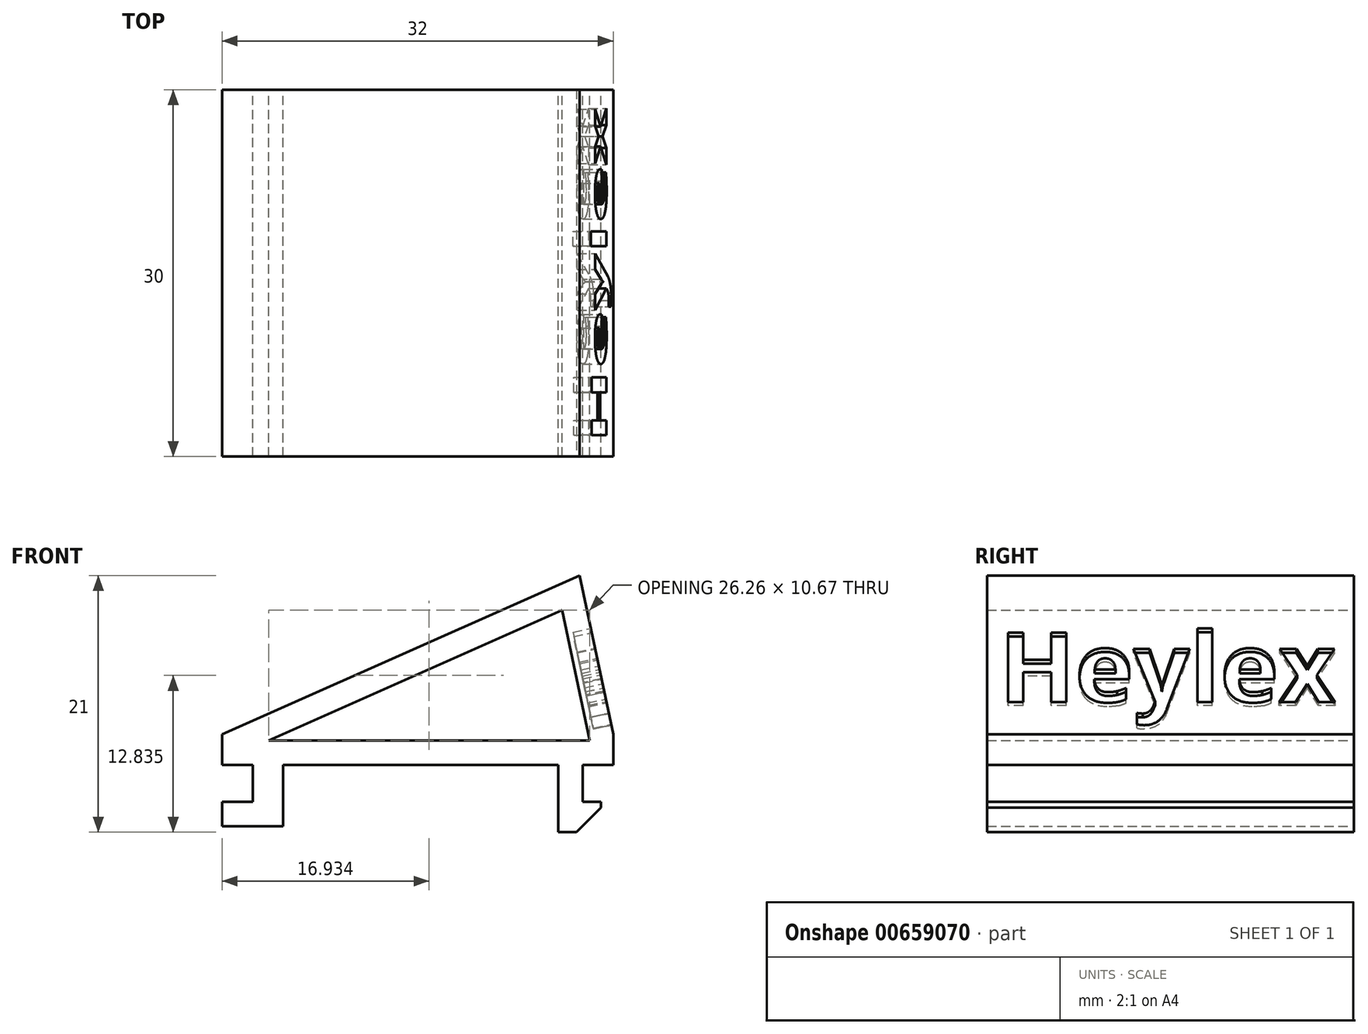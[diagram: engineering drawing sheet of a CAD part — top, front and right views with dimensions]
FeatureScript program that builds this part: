
annotation { "Feature Type Name" : "Feature", "Feature Type Description" : "" }
export const myFeature = defineFeature(function(context is Context, id is Id, definition is map)
    precondition{}
    {
        {
            var Q0;
            Q0=qCreatedBy(makeId("Front.planeOp"),FACE);
            var sketch = newSketch(context, id + "F0", { "sketchPlane" : qUnion([Q0])});
            skLineSegment(sketch, "E0.left", {"start": v(-16.03, 0) * mm, "end": v(-16.03, 2.5) * mm});
            skLineSegment(sketch, "E0.right", {"start": v(15.97, 0) * mm, "end": v(15.97, 2.5) * mm});
            skLineSegment(sketch, "E1", {"start": v(-16.03, 2.5) * mm, "end": v(13.21, 15.5) * mm});
            skLineSegment(sketch, "E2", {"start": v(13.21, 15.5) * mm, "end": v(15.97, 2.5) * mm});
            skLineSegment(sketch, "E3", {"start": v(-16.03, 0) * mm, "end": v(-13.53, 0) * mm});
            skLineSegment(sketch, "E4", {"start": v(-13.53, 0) * mm, "end": v(-13.53, -3) * mm});
            skLineSegment(sketch, "E5", {"start": v(-13.53, -3) * mm, "end": v(-16.03, -3) * mm});
            skLineSegment(sketch, "E6", {"start": v(-16.03, -3) * mm, "end": v(-16.03, -5) * mm});
            skLineSegment(sketch, "E7", {"start": v(-16.03, -5) * mm, "end": v(-11.03, -5) * mm});
            skLineSegment(sketch, "E8", {"start": v(-11.03, -5) * mm, "end": v(-11.03, 0) * mm});
            skLineSegment(sketch, "E9", {"start": v(-11.03, 0) * mm, "end": v(11.47, 0) * mm});
            skLineSegment(sketch, "E10", {"start": v(11.47, 0) * mm, "end": v(11.47, -5.5) * mm});
            skLineSegment(sketch, "E11", {"start": v(11.47, -5.5) * mm, "end": v(14.97, -5.5) * mm});
            skLineSegment(sketch, "E12", {"start": v(14.97, -5.5) * mm, "end": v(14.97, -3) * mm});
            skLineSegment(sketch, "E13", {"start": v(14.97, -3) * mm, "end": v(13.47, -3) * mm});
            skLineSegment(sketch, "E14", {"start": v(13.47, -3) * mm, "end": v(13.47, 0) * mm});
            skLineSegment(sketch, "E15", {"start": v(13.47, 0) * mm, "end": v(15.97, 0) * mm});
            skLineSegment(sketch, "E16.0", {"start": v(-12.23, 2) * mm, "end": v(11.77, 12.67) * mm});
            skLineSegment(sketch, "E16.1", {"start": v(-12.23, 2) * mm, "end": v(13.97, 2) * mm});
            skLineSegment(sketch, "E16.2", {"start": v(13.97, 2) * mm, "end": v(14.04, 2) * mm});
            skLineSegment(sketch, "E16.3", {"start": v(11.77, 12.67) * mm, "end": v(14.04, 2) * mm});
            skSolve(sketch);
        }
        {
            var Q0;
            Q0=makeQuery(id+"F0.imprint","IMPRINT",FACE,{"disambiguationData":[TD([[makeQuery(id+"F0.imprint","IMPRINT",EDGE,{"derivedFrom":sQuery(id+"F0.wireOp",EDGE,"E0.left")}),-1.0]])]});
            extrude(context, id + "F1", {"entities" : qUnion([Q0]), "depth" : 30 * mm, "offsetDistance" : 25 * mm});
        }
        {
            var Q0;
            Q0=makeQuery(id+"F1.opExtrude","SWEPT_EDGE",EDGE,{"disambiguationData":[OSD([sQuery(id+"F0.wireOp",EDGE,"E11"),sQuery(id+"F0.wireOp",EDGE,"E12")])]});
            chamfer(context, id + "F2", {"entities" : qUnion([Q0]), "width" : 2 * mm, "tangentPropagation" : true});
        }
        {
            var Q0;
            Q0=makeQuery(id+"F1.opExtrude","SWEPT_FACE",FACE,{"disambiguationData":[OSD([sQuery(id+"F0.wireOp",EDGE,"E2")])]});
            var sketch = newSketch(context, id + "F3", { "sketchPlane" : qUnion([Q0])});
            skText(sketch, "E17", { "text": "Heylex", "fontName": "OpenSans-Bold.ttf"});
            const initialGuessF3  = {"E17": [-0.029, 0.00185, 1, 0, 0.00583]};
            skSetInitialGuess(sketch, initialGuessF3);
            skSolve(sketch);
        }
        {
            var Q0;
            Q0 = qSketchRegion(id + "F3", true);
            extrude(context, id + "F4", {"entities" : qUnion([Q0]), "operationType" : NewBodyOperationType.REMOVE, "oppositeDirection" : true, "depth" : 1.5 * mm, "offsetDistance" : 25 * mm});
        }
    });
